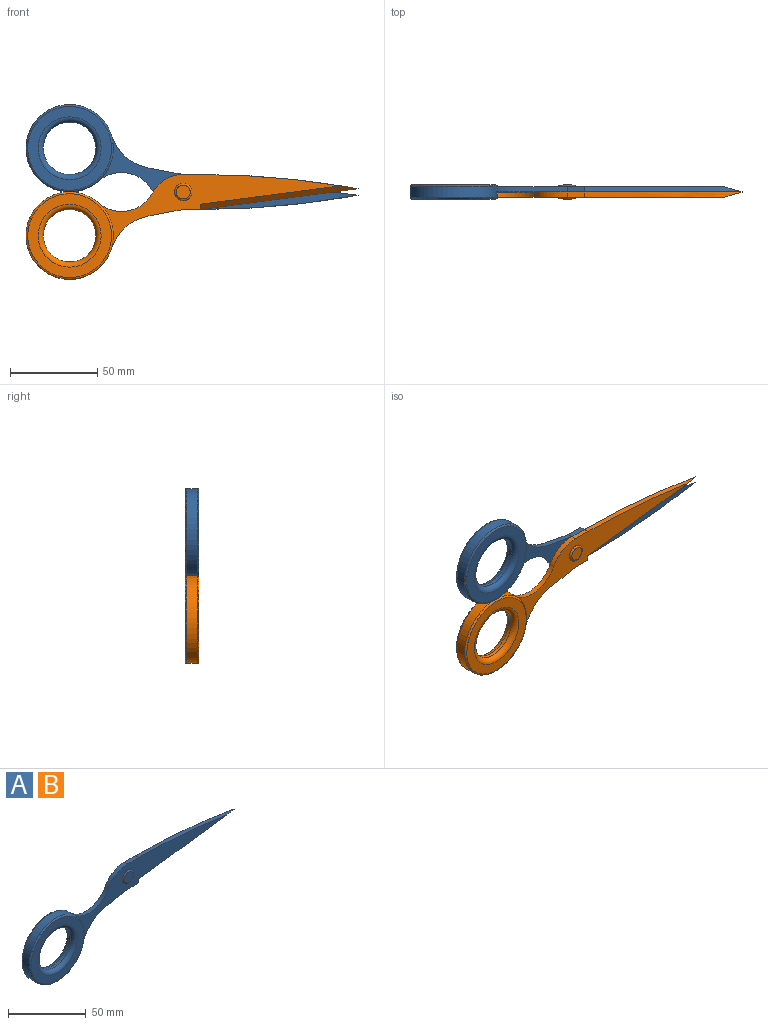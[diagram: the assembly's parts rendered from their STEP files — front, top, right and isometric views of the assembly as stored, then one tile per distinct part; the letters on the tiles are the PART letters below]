
ASSEMBLY  parts=2 mates=1
PART A: 20 faces, bbox 192.1x8x62.1 mm
  f0: plane 138.64x43.21mm, normal (0,-1,0), area 1463.3mm2, adj f2,f3,f4,f5,f7,f8,f13,f14
  f1: plane 148.5x43.21mm, normal (0,1,0), area 1797.2mm2, adj f2,f3,f4,f5,f6,f7,f8,f13
  f2: plane 10x3mm, normal (0,0,-1), area 30mm2, adj f0,f1,f7,f14
  f3: cylinder r=500mm len=90mm, axis (0,1,0), area 256.6mm2, adj f0,f1,f4,f13
  f4: plane 10x3mm, normal (0,0,1), area 30mm2, adj f0,f1,f3,f8
  f5: cylinder r=20mm len=30.85mm, axis (0,1,0), area 108.1mm2, adj f0,f1,f6,f8
  f6: cylinder r=25mm len=50mm, axis (0,1,0), area 853.6mm2, adj f1,f5,f7,f17,f18
  f7: extruded ~41.39x23.21mm, area 152.1mm2, adj f0,f1,f2,f6
  f8: cylinder r=20mm len=17.65mm, axis (0,1,0), area 64.9mm2, adj f0,f1,f4,f5
  f9: plane 48x48mm, normal (0,1,0), area 791.7mm2, adj f16,f17
  f10: cylinder r=15mm len=30mm, axis (0,1,0), area 188.5mm2, adj f15,f16
  f11: plane 48x48mm, normal (0,-1,0), area 791.7mm2, adj f15,f18
  f12: plane 8x8mm, normal (0,-1,0), area 50.3mm2, adj f19
  f13: plane 90x13.54mm, normal (0.09,-0.7,-0.7), area 362.7mm2, adj f0,f1,f3,f14
  f14: plane 3x3mm, normal (1,0,0), area 4.5mm2, adj f0,f2,f13
  f15: torus R=18mm, axis (0,-1,0), area 476.4mm2, adj f10,f11
  f16: torus R=18mm, axis (0,-1,0), area 476.4mm2, adj f9,f10
  f17: torus R=24mm, axis (0,-1,0), area 243.2mm2, adj f6,f9
  f18: torus R=24mm, axis (0,-1,0), area 243.2mm2, adj f0,f6,f11
  f19: torus R=4mm, axis (0,-1,0), area 45.8mm2, adj f0,f12
PART B: same geometry as A
PLACE A rot(axis=(1,0,0),180deg) t=(0,0,0)mm
PLACE B at identity fixed
MATE revolute B.f19 <-> A.f19  axis (0,-1,0) through (0,0,0)mm
